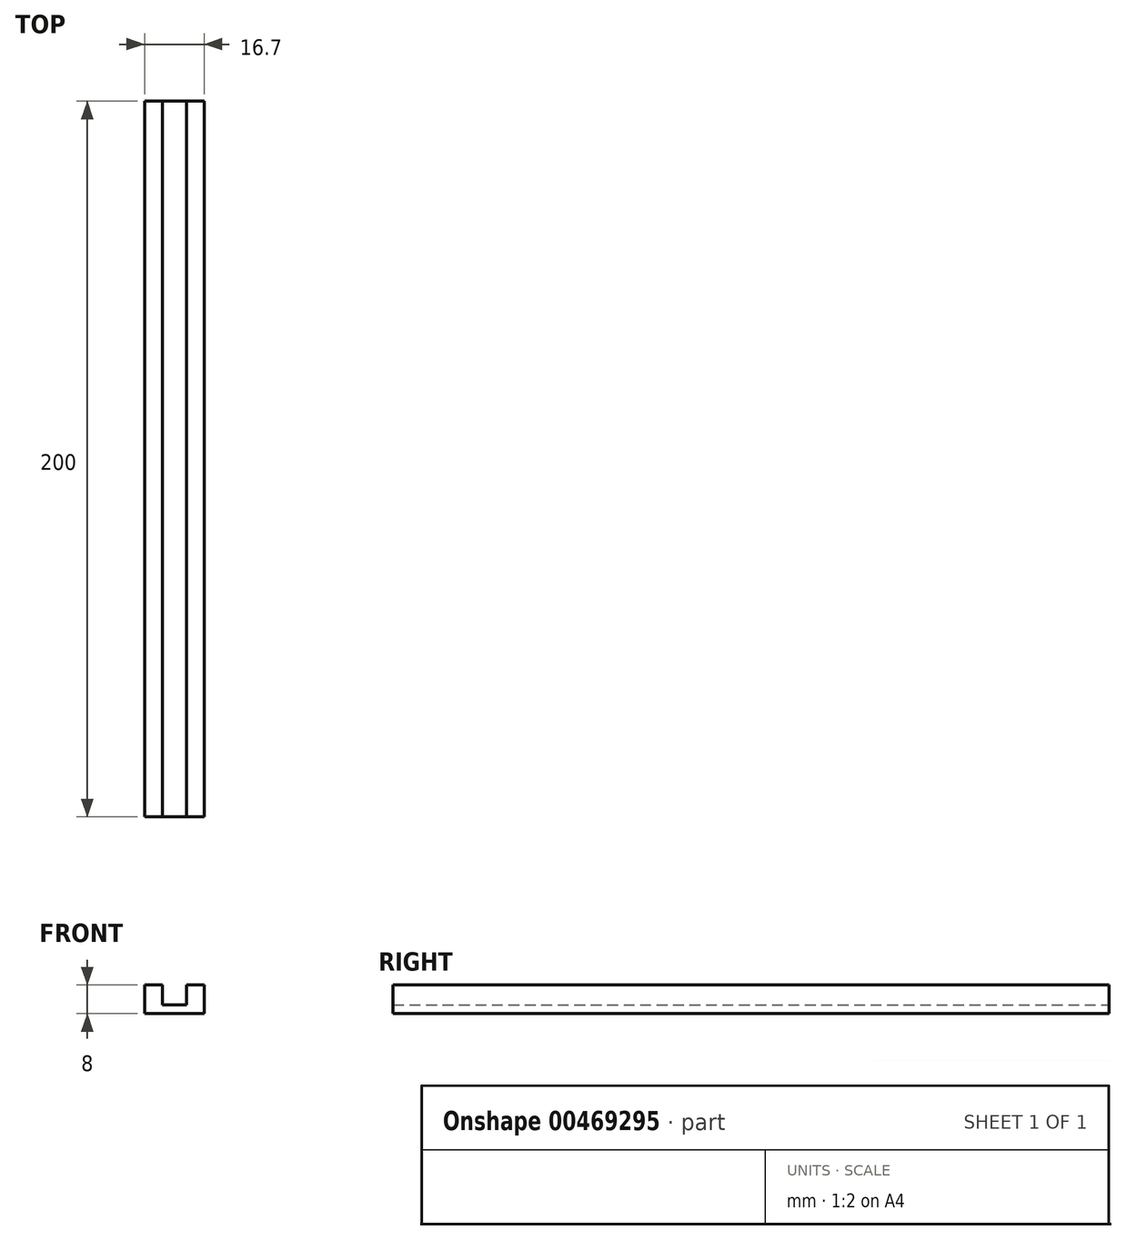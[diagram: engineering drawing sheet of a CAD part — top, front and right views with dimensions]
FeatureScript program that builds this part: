
annotation { "Feature Type Name" : "Feature", "Feature Type Description" : "" }
export const myFeature = defineFeature(function(context is Context, id is Id, definition is map)
    precondition{}
    {
        {
            var Q0;
            Q0=qCreatedBy(makeId("Front.planeOp"),FACE);
            var sketch = newSketch(context, id + "F0", { "sketchPlane" : qUnion([Q0])});
            skLineSegment(sketch, "E0.bottom", {"start": v(-8.35, 4) * mm, "end": v(-3.35, 4) * mm});
            skLineSegment(sketch, "E0.top", {"start": v(-8.35, -4) * mm, "end": v(8.35, -4) * mm});
            skLineSegment(sketch, "E0.left", {"start": v(-8.35, 4) * mm, "end": v(-8.35, -4) * mm});
            skLineSegment(sketch, "E0.right", {"start": v(8.35, 4) * mm, "end": v(8.35, -4) * mm});
            skPoint(sketch, "E0.middle", {"position": v(0, 0) * mm});
            skLineSegment(sketch, "E1.top", {"start": v(-3.35, -2) * mm, "end": v(3.35, -2) * mm});
            skLineSegment(sketch, "E1.left", {"start": v(-3.35, 4) * mm, "end": v(-3.35, -2) * mm});
            skLineSegment(sketch, "E1.right", {"start": v(3.35, 4) * mm, "end": v(3.35, -2) * mm});
            skLineSegment(sketch, "E2.trimOffspring", {"start": v(3.35, 4) * mm, "end": v(8.35, 4) * mm});
            skSolve(sketch);
        }
        {
            var Q0;
            Q0 = qSketchRegion(id + "F0", true);
            extrude(context, id + "F1", {"entities" : qUnion([Q0]), "depth" : 10 * mm});
        }
        {
            var Q0;
            Q0=makeQuery(id+"F1.opExtrude","SWEPT_FACE",FACE,{"disambiguationData":[OSD([sQuery(id+"F0.wireOp",EDGE,"E1.top")])]});
            extrude(context, id + "F2", {"entities" : qUnion([Q0]), "operationType" : NewBodyOperationType.ADD, "depth" : 0.5 * mm});
        }
        {
            var Q0;
            {var subQ0=sQuery(id+"F0.wireOp",EDGE,"E1.top");Q0=makeQuery(id+"F2.boolean.opBoolean","MERGE",FACE,{"derivedFrom":[makeQuery(id+"F1.opExtrude","CAP_FACE",FACE,{"disambiguationData":[OSD([sQuery(id+"F0.wireOp",EDGE,"E0.bottom"),sQuery(id+"F0.wireOp",EDGE,"E0.top"),sQuery(id+"F0.wireOp",EDGE,"E0.left"),sQuery(id+"F0.wireOp",EDGE,"E0.right"),subQ0,sQuery(id+"F0.wireOp",EDGE,"E1.left"),sQuery(id+"F0.wireOp",EDGE,"E1.right"),sQuery(id+"F0.wireOp",EDGE,"E2.trimOffspring")])],"isStart":false}),makeQuery(id+"F2.opExtrude","SWEPT_FACE",FACE,{"disambiguationData":[OSD([subQ0]),TDD([makeQuery(id+"F1.opExtrude","CAP_EDGE",EDGE,{"disambiguationData":[OSD([subQ0])],"isStart":false})])]})]});}
            extrude(context, id + "F3", {"entities" : qUnion([Q0]), "operationType" : NewBodyOperationType.ADD, "depth" : 190 * mm});
        }
    });
